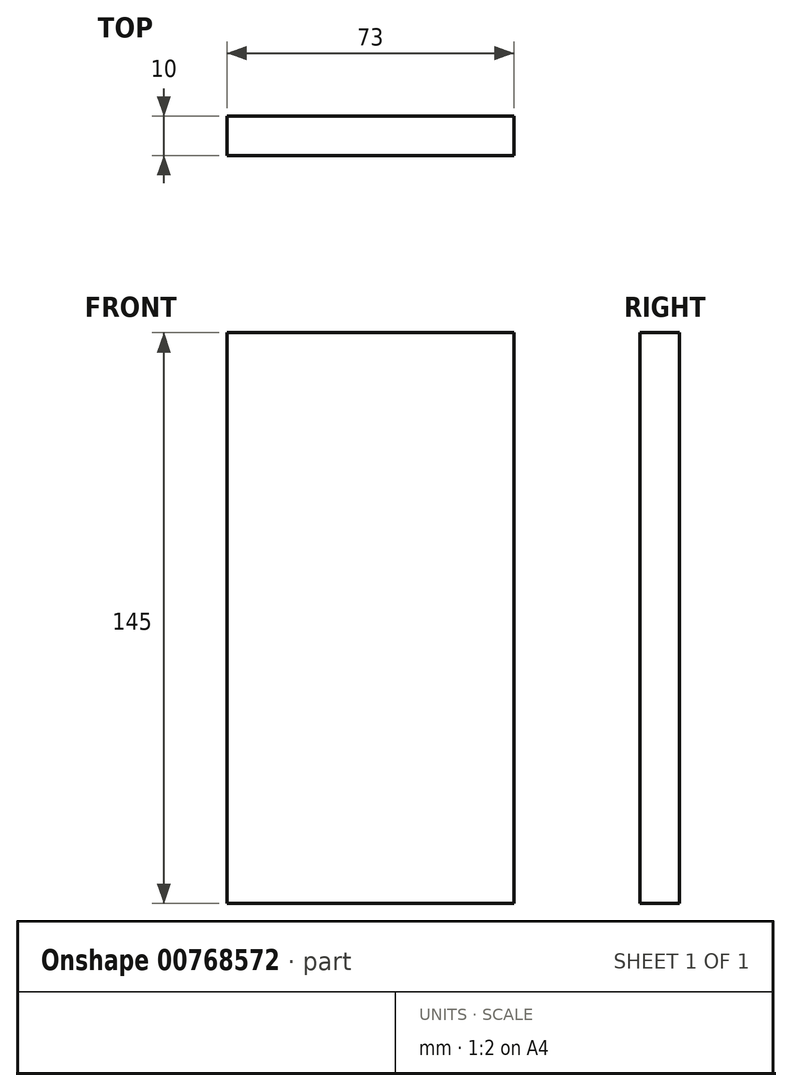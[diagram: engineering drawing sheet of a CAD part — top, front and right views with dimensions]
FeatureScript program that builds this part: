
annotation { "Feature Type Name" : "Feature", "Feature Type Description" : "" }
export const myFeature = defineFeature(function(context is Context, id is Id, definition is map)
    precondition{}
    {
        {
            var Q0;
            Q0=qCreatedBy(makeId("Front.planeOp"),FACE);
            var sketch = newSketch(context, id + "F0", { "sketchPlane" : qUnion([Q0])});
            skLineSegment(sketch, "E0", {"start": v(0, 0) * mm, "end": v(0, 145) * mm});
            skLineSegment(sketch, "E1", {"start": v(0, 145) * mm, "end": v(73, 145) * mm});
            skLineSegment(sketch, "E2", {"start": v(73, 145) * mm, "end": v(73, 0) * mm});
            skLineSegment(sketch, "E3", {"start": v(73, 0) * mm, "end": v(0, 0) * mm});
            skSolve(sketch);
        }
        {
            var Q0;
            Q0=makeQuery(id+"F0.imprint","IMPRINT",FACE,{"disambiguationData":[TD([[makeQuery(id+"F0.imprint","IMPRINT",EDGE,{"derivedFrom":sQuery(id+"F0.wireOp",EDGE,"E0")}),-1.0]])]});
            extrude(context, id + "F1", {"entities" : qUnion([Q0]), "depth" : 10 * mm, "offsetDistance" : 25 * mm});
        }
    });
